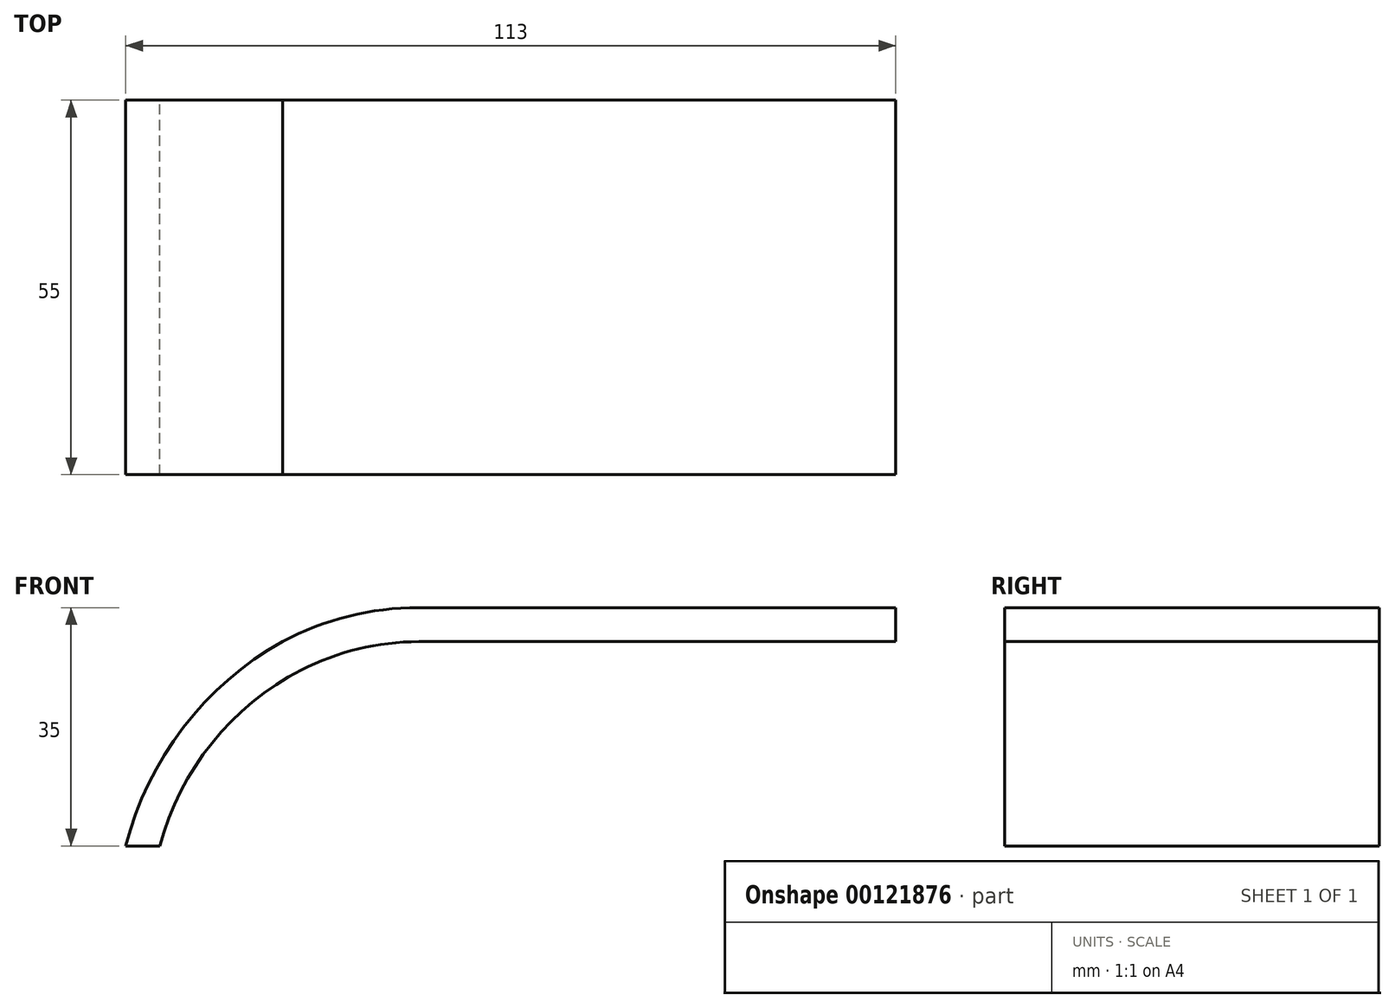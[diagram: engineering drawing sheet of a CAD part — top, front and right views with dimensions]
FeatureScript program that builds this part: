
annotation { "Feature Type Name" : "Feature", "Feature Type Description" : "" }
export const myFeature = defineFeature(function(context is Context, id is Id, definition is map)
    precondition{}
    {
        {
            var Q0;
            Q0=qCreatedBy(makeId("Front.planeOp"),FACE);
            var sketch = newSketch(context, id + "F0", { "sketchPlane" : qUnion([Q0])});
            skLineSegment(sketch, "E0", {"start": v(-40.09, 17.26) * mm, "end": v(29.91, 17.26) * mm});
            skArc(sketch, "E1", {"start": v(-40.09, 17.26) * mm, "mid": v(-50.4, 15.99) * mm, "end": v(-60.09, 12.26) * mm});
            skArc(sketch, "E2", {"start": v(-60.09, 12.26) * mm, "mid": v(-74.67, -0.38) * mm, "end": v(-83.09, -17.74) * mm});
            skLineSegment(sketch, "E3", {"start": v(29.91, 17.26) * mm, "end": v(29.91, 12.26) * mm});
            skLineSegment(sketch, "E4", {"start": v(-40.09, 17.26) * mm, "end": v(-40.09, 12.26) * mm});
            skLineSegment(sketch, "E5", {"start": v(-60.09, 12.26) * mm, "end": v(-57.33, 8.08) * mm});
            skLineSegment(sketch, "E6", {"start": v(-83.09, -17.74) * mm, "end": v(-78.09, -17.74) * mm});
            skLineSegment(sketch, "E7", {"start": v(-40.09, 12.26) * mm, "end": v(29.91, 12.26) * mm});
            skArc(sketch, "E8", {"start": v(-40.09, 12.26) * mm, "mid": v(-48.96, 11.2) * mm, "end": v(-57.33, 8.08) * mm});
            skArc(sketch, "E9", {"start": v(-57.33, 8.08) * mm, "mid": v(-70.44, -2.63) * mm, "end": v(-78.09, -17.74) * mm});
            skSolve(sketch);
        }
        {
            var Q0;
            Q0=makeQuery(id+"F0.imprint","IMPRINT",FACE,{"disambiguationData":[TD([[makeQuery(id+"F0.imprint","IMPRINT",EDGE,{"derivedFrom":sQuery(id+"F0.wireOp",EDGE,"E2")}),1.0]])]});
            var Q1;
            Q1=makeQuery(id+"F0.imprint","IMPRINT",FACE,{"disambiguationData":[TD([[makeQuery(id+"F0.imprint","IMPRINT",EDGE,{"derivedFrom":sQuery(id+"F0.wireOp",EDGE,"E1")}),1.0]])]});
            var Q2;
            Q2=makeQuery(id+"F0.imprint","IMPRINT",FACE,{"disambiguationData":[TD([[makeQuery(id+"F0.imprint","IMPRINT",EDGE,{"derivedFrom":sQuery(id+"F0.wireOp",EDGE,"E0")}),-1.0]])]});
            extrude(context, id + "F1", {"entities" : qUnion([Q0, Q1, Q2]), "depth" : 55 * mm});
        }
    });
